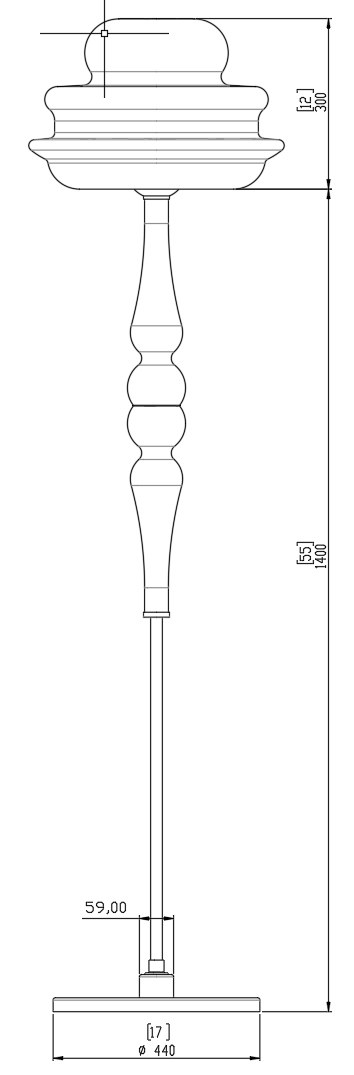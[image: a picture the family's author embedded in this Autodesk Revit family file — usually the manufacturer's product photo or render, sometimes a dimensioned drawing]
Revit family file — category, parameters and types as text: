
# Revit family: PEGGY-Wall
name_source: partatom
category: Lighting Fixtures
units: mm (PartAtom-declared; Revit-internal decimal feet)

## family parameters
Always vertical = Yes
Cut with Voids When Loaded = No
Host = Wall
Light Source = No
OmniClass Number = 23.80.70.00
OmniClass Title = Lighting
Part Type = Normal
Room Calculation Point = No
Round Connector Dimension = Use Diameter
Shared = No

## types (1)
- PEGGY AP
    Bulb Diametr = 15 mm  [stored 0.0492126 ft]
    Country = Europe
    Default Elevation = 0 mm  [stored 0 ft]
    Depth = 108 mm
    Description = WALL LAMP
    Designer = Hangar Design Group
    Manufacturer = Vistosi
    Manufacturer country = Italy
    Model = PEGGY
    Type Comments = Hangar Design Group
    URL = https://vistosi.com
    URL Product Page = https://vistosi.it
    Width = 108 mm

note: [stored X ft] marks values corroborated as IEEE doubles in the binary element streams (Revit-internal decimal feet)

## geometry (parser evidence)
native form markers: Sweep x9
no freeform markers — native parametric forms only
